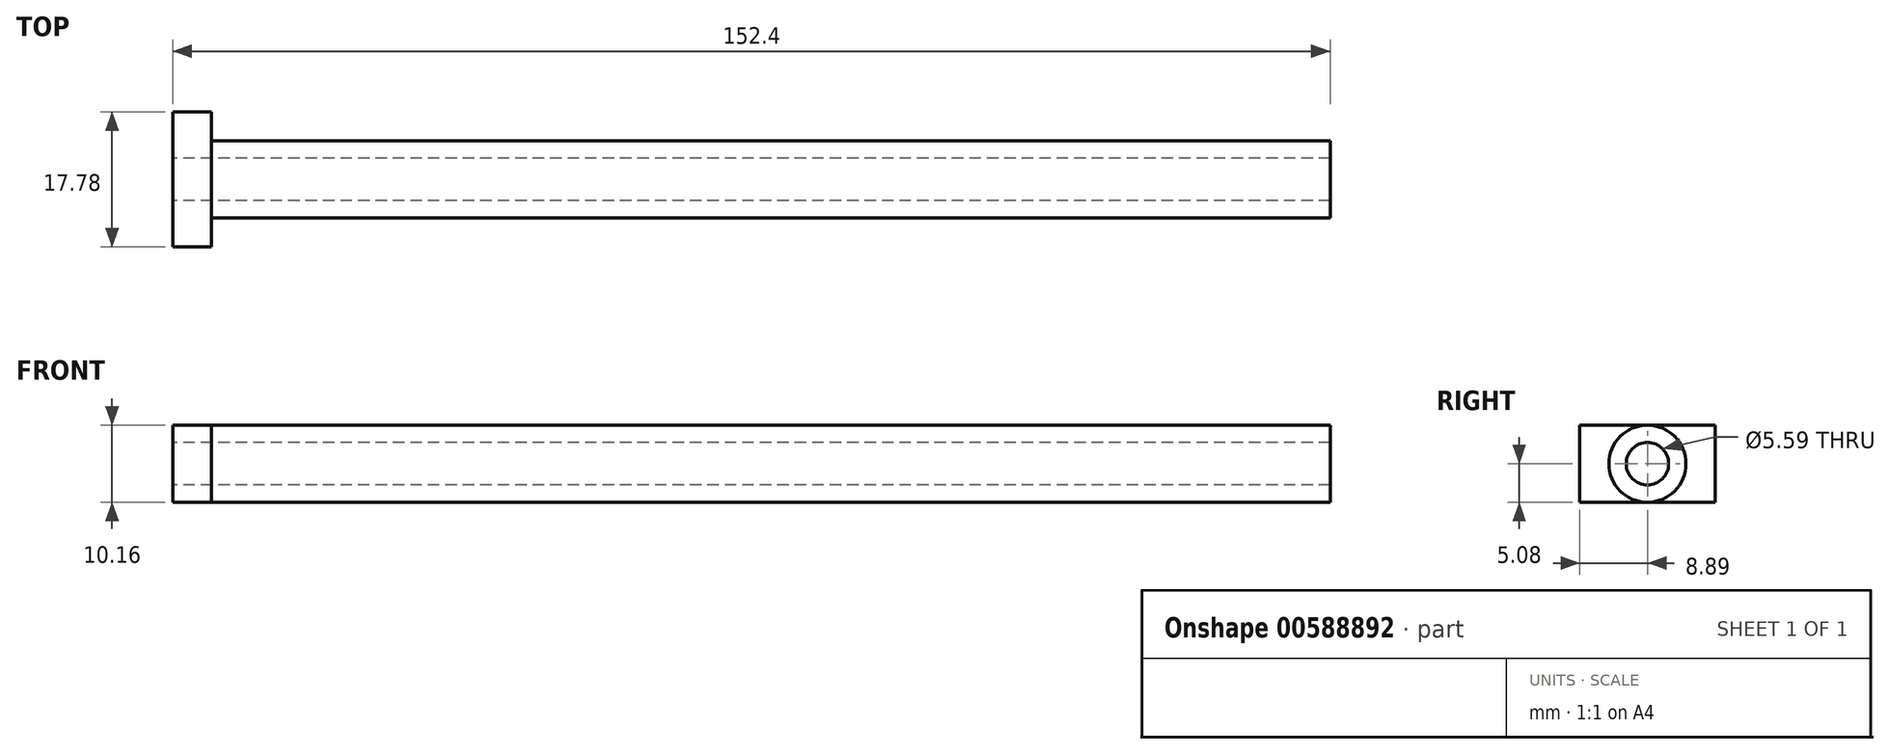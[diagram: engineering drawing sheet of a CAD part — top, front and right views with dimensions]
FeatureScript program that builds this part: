
annotation { "Feature Type Name" : "Feature", "Feature Type Description" : "" }
export const myFeature = defineFeature(function(context is Context, id is Id, definition is map)
    precondition{}
    {
        {
            var Q0;
            Q0=qCreatedBy(makeId("Right.planeOp"),FACE);
            var sketch = newSketch(context, id + "F0", { "sketchPlane" : qUnion([Q0])});
            skCircle(sketch, "E0", {"center": v(0, 0) * mm, "radius": 2.8 * mm});
            skCircle(sketch, "E1", {"center": v(0, 0) * mm, "radius": 5.08 * mm});
            skSolve(sketch);
        }
        {
            var Q0;
            Q0 = qSketchRegion(id + "F0", true);
            extrude(context, id + "F1", {"entities" : qUnion([Q0]), "depth" : 152.4 * mm, "offsetDistance" : 25.4 * mm});
        }
        {
            var Q0;
            Q0=qCreatedBy(makeId("Right.planeOp"),FACE);
            var sketch = newSketch(context, id + "F2", { "sketchPlane" : qUnion([Q0])});
            skLineSegment(sketch, "E2", {"start": v(8.9, -5.08) * mm, "end": v(-8.89, -5.08) * mm});
            skLineSegment(sketch, "E3", {"start": v(-8.89, -5.08) * mm, "end": v(-8.9, 5.08) * mm});
            skLineSegment(sketch, "E4", {"start": v(-8.9, 5.08) * mm, "end": v(8.9, 5.08) * mm});
            skLineSegment(sketch, "E5", {"start": v(8.9, 5.08) * mm, "end": v(8.9, -5.08) * mm});
            skCircle(sketch, "E6", {"center": v(0, 0) * mm, "radius": 5.08 * mm});
            skSolve(sketch);
        }
        {
            var Q0;
            {var subQ0=sQuery(id+"F2.wireOp",EDGE,"E3");Q0=makeQuery(id+"F2.imprint","IMPRINT",FACE,{"disambiguationData":[TD([[makeQuery(id+"F2.imprint","IMPRINT",EDGE,{"derivedFrom":subQ0}),-1.0]])]});}
            var Q1;
            {var subQ0=sQuery(id+"F2.wireOp",EDGE,"E5");Q1=makeQuery(id+"F2.imprint","IMPRINT",FACE,{"disambiguationData":[TD([[makeQuery(id+"F2.imprint","IMPRINT",EDGE,{"derivedFrom":subQ0}),-1.0]])]});}
            extrude(context, id + "F3", {"entities" : qUnion([Q0, Q1]), "operationType" : NewBodyOperationType.ADD, "depth" : 5.08 * mm, "offsetDistance" : 25.4 * mm});
        }
    });
